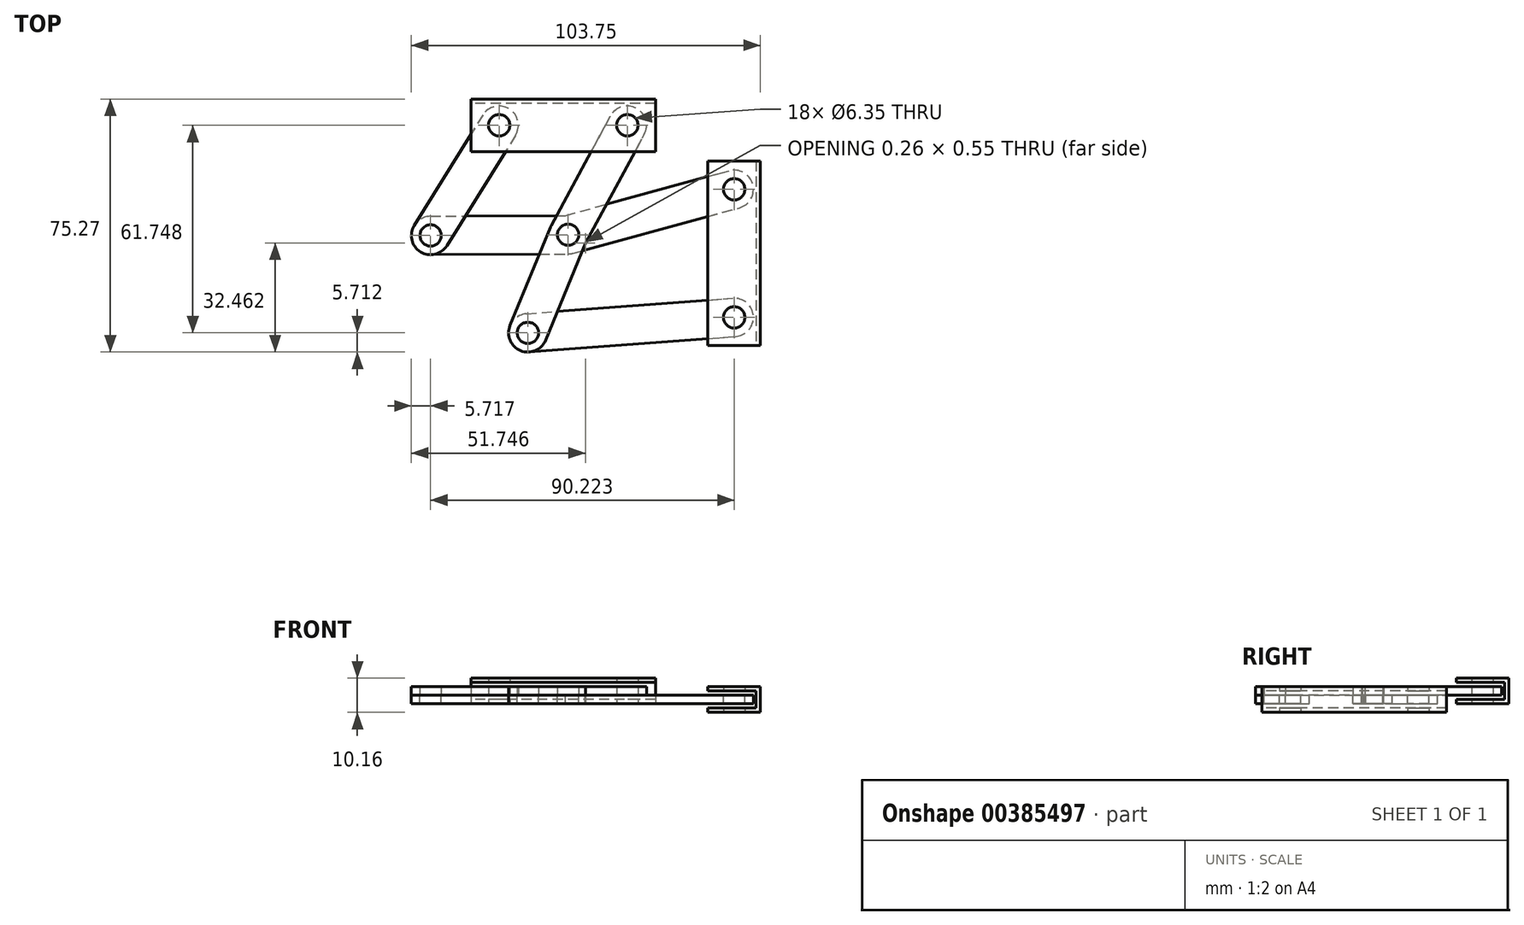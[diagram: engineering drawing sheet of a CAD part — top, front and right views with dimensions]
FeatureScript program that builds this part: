
annotation { "Feature Type Name" : "Feature", "Feature Type Description" : "" }
export const myFeature = defineFeature(function(context is Context, id is Id, definition is map)
    precondition{}
    {
        {
            var Q0;
            Q0=qCreatedBy(makeId("Top.planeOp"),FACE);
            var sketch = newSketch(context, id + "F0", { "sketchPlane" : qUnion([Q0])});
            skCircle(sketch, "E0", {"center": v(-19.05, 0) * mm, "radius": 3.18 * mm});
            skCircle(sketch, "E1", {"center": v(19.05, 0) * mm, "radius": 3.18 * mm});
            skCircle(sketch, "E2", {"center": v(50.8, -19.05) * mm, "radius": 3.18 * mm});
            skCircle(sketch, "E3", {"center": v(50.8, -57.15) * mm, "radius": 3.18 * mm});
            skLineSegment(sketch, "E4", {"start": v(-19.05, 0) * mm, "end": v(19.05, 0) * mm, "construction": true});
            skLineSegment(sketch, "E5", {"start": v(50.8, -19.05) * mm, "end": v(50.8, -57.15) * mm, "construction": true});
            skPoint(sketch, "E6", {"position": v(50.8, -38.1) * mm});
            skPoint(sketch, "E7", {"position": v(0, 0) * mm});
            skSolve(sketch);
        }
        {
            var Q0;
            Q0=qCreatedBy(makeId("Top.planeOp"),FACE);
            var sketch = newSketch(context, id + "F1", { "sketchPlane" : qUnion([Q0])});
            skCircle(sketch, "E8.0", {"center": v(-19.05, 0) * mm, "radius": 3.18 * mm});
            skCircle(sketch, "E9", {"center": v(-39.42, -32.79) * mm, "radius": 3.18 * mm});
            skCircle(sketch, "E10", {"center": v(-19.05, 0) * mm, "radius": 5.72 * mm});
            skCircle(sketch, "E11", {"center": v(-39.42, -32.79) * mm, "radius": 5.72 * mm});
            skLineSegment(sketch, "E12", {"start": v(-23.9, 3.02) * mm, "end": v(-44.28, -29.77) * mm});
            skLineSegment(sketch, "E13", {"start": v(-14.2, -3.02) * mm, "end": v(-34.57, -35.8) * mm});
            skCircle(sketch, "E14.0", {"center": v(50.8, -57.15) * mm, "radius": 3.18 * mm});
            skCircle(sketch, "E15", {"center": v(-10.51, -61.75) * mm, "radius": 3.18 * mm});
            skCircle(sketch, "E16", {"center": v(-10.51, -61.75) * mm, "radius": 5.72 * mm});
            skCircle(sketch, "E17", {"center": v(50.8, -57.15) * mm, "radius": 5.72 * mm});
            skLineSegment(sketch, "E18", {"start": v(-10.94, -56.05) * mm, "end": v(50.37, -51.45) * mm});
            skLineSegment(sketch, "E19", {"start": v(-10.09, -67.45) * mm, "end": v(51.23, -62.85) * mm});
            skCircle(sketch, "E20.0", {"center": v(19.05, 0) * mm, "radius": 3.18 * mm});
            skCircle(sketch, "E21.0", {"center": v(50.8, -19.05) * mm, "radius": 3.18 * mm});
            skCircle(sketch, "E22", {"center": v(19.05, 0) * mm, "radius": 5.72 * mm});
            skCircle(sketch, "E23", {"center": v(50.8, -19.05) * mm, "radius": 5.72 * mm});
            skCircle(sketch, "E24", {"center": v(1.45, -32.56) * mm, "radius": 3.18 * mm});
            skCircle(sketch, "E25", {"center": v(1.45, -32.56) * mm, "radius": 5.72 * mm});
            skLineSegment(sketch, "E26", {"start": v(-3.58, -29.84) * mm, "end": v(14.02, 2.72) * mm});
            skLineSegment(sketch, "E27", {"start": v(6.48, -35.27) * mm, "end": v(24.08, -2.72) * mm});
            skLineSegment(sketch, "E28", {"start": v(2.96, -38.07) * mm, "end": v(52.3, -24.56) * mm});
            skLineSegment(sketch, "E29", {"start": v(-0.06, -27.04) * mm, "end": v(49.3, -13.54) * mm});
            skLineSegment(sketch, "E30", {"start": v(-39.4, -38.5) * mm, "end": v(1.48, -38.27) * mm});
            skLineSegment(sketch, "E31", {"start": v(-39.46, -27.07) * mm, "end": v(1.42, -26.84) * mm});
            skLineSegment(sketch, "E32", {"start": v(-5.22, -63.92) * mm, "end": v(6.74, -34.72) * mm});
            skLineSegment(sketch, "E33", {"start": v(-3.84, -30.39) * mm, "end": v(-15.8, -59.58) * mm});
            skSolve(sketch);
        }
        {
            var Q0;
            {var subQ1=sQuery(id+"F1.wireOp",EDGE,"E22");var subQ8=sQuery(id+"F1.wireOp",EDGE,"E26");var subQ10=makeQuery(id+"F1.imprint","INTERSECT",VERTEX,{"derivedFrom":[subQ1,subQ8]});Q0=makeQuery(id+"F1.imprint","IMPRINT",FACE,{"disambiguationData":[TD([[makeQuery(id+"F1.imprint","IMPRINT",EDGE,{"disambiguationData":[TD([[subQ10,-1.0]])],"derivedFrom":subQ1}),-1.0]])]});}
            var Q1;
            {var subQ0=sQuery(id+"F1.wireOp",EDGE,"E26");var subQ1=sQuery(id+"F1.wireOp",EDGE,"E25");var subQ2=makeQuery(id+"F1.imprint","INTERSECT",VERTEX,{"derivedFrom":[subQ1,subQ0]});Q1=makeQuery(id+"F1.imprint","IMPRINT",FACE,{"disambiguationData":[TD([[makeQuery(id+"F1.imprint","IMPRINT",EDGE,{"disambiguationData":[TD([[subQ2,1.0]])],"derivedFrom":subQ1}),-1.0]])]});}
            var Q2;
            {var subQ0=sQuery(id+"F1.wireOp",EDGE,"E28");var subQ1=sQuery(id+"F1.wireOp",EDGE,"E25");var subQ2=makeQuery(id+"F1.imprint","INTERSECT",VERTEX,{"derivedFrom":[subQ1,subQ0]});Q2=makeQuery(id+"F1.imprint","IMPRINT",FACE,{"disambiguationData":[TD([[makeQuery(id+"F1.imprint","IMPRINT",EDGE,{"disambiguationData":[TD([[subQ2,1.0]])],"derivedFrom":subQ1}),-1.0]])]});}
            var Q3;
            {var subQ0=sQuery(id+"F1.wireOp",EDGE,"E28");var subQ1=sQuery(id+"F1.wireOp",EDGE,"E25");var subQ2=makeQuery(id+"F1.imprint","INTERSECT",VERTEX,{"derivedFrom":[subQ1,subQ0]});Q3=makeQuery(id+"F1.imprint","IMPRINT",FACE,{"disambiguationData":[TD([[makeQuery(id+"F1.imprint","IMPRINT",EDGE,{"disambiguationData":[TD([[subQ2,-1.0]])],"derivedFrom":subQ1}),-1.0]])]});}
            var Q4;
            {var subQ5=sQuery(id+"F1.wireOp",EDGE,"E25");var subQ7=sQuery(id+"F1.wireOp",EDGE,"E27");var subQ8=makeQuery(id+"F1.imprint","INTERSECT",VERTEX,{"derivedFrom":[subQ5,subQ7]});Q4=makeQuery(id+"F1.imprint","IMPRINT",FACE,{"disambiguationData":[TD([[makeQuery(id+"F1.imprint","IMPRINT",EDGE,{"disambiguationData":[TD([[subQ8,1.0]])],"derivedFrom":subQ5}),-1.0]])]});}
            var Q5;
            {var subQ7=sQuery(id+"F1.wireOp",EDGE,"E18");var subQ9=sQuery(id+"F1.wireOp",EDGE,"E16");var subQ10=makeQuery(id+"F1.imprint","INTERSECT",VERTEX,{"derivedFrom":[subQ9,subQ7]});Q5=makeQuery(id+"F1.imprint","IMPRINT",FACE,{"disambiguationData":[TD([[makeQuery(id+"F1.imprint","IMPRINT",EDGE,{"disambiguationData":[TD([[subQ10,-1.0]])],"derivedFrom":subQ9}),-1.0]])]});}
            var Q6;
            {var subQ0=sQuery(id+"F1.wireOp",EDGE,"E29");var subQ1=sQuery(id+"F1.wireOp",EDGE,"E25");var subQ2=makeQuery(id+"F1.imprint","INTERSECT",VERTEX,{"derivedFrom":[subQ1,subQ0]});Q6=makeQuery(id+"F1.imprint","IMPRINT",FACE,{"disambiguationData":[TD([[makeQuery(id+"F1.imprint","IMPRINT",EDGE,{"disambiguationData":[TD([[subQ2,1.0]])],"derivedFrom":subQ1}),-1.0]])]});}
            var Q7;
            {var subQ0=sQuery(id+"F1.wireOp",EDGE,"E18");var subQ1=sQuery(id+"F1.wireOp",EDGE,"E16");var subQ2=makeQuery(id+"F1.imprint","INTERSECT",VERTEX,{"derivedFrom":[subQ1,subQ0]});Q7=makeQuery(id+"F1.imprint","IMPRINT",FACE,{"disambiguationData":[TD([[makeQuery(id+"F1.imprint","IMPRINT",EDGE,{"disambiguationData":[TD([[subQ2,1.0]])],"derivedFrom":subQ1}),-1.0]])]});}
            var Q8;
            Q8=makeQuery(id+"F1.imprint","IMPRINT",FACE,{"disambiguationData":[TD([[makeQuery(id+"F1.imprint","IMPRINT",EDGE,{"derivedFrom":sQuery(id+"F1.wireOp",EDGE,"E15")}),-1.0]])]});
            var Q9;
            Q9=makeQuery(id+"F1.imprint","IMPRINT",FACE,{"disambiguationData":[TD([[makeQuery(id+"F1.imprint","IMPRINT",EDGE,{"derivedFrom":sQuery(id+"F1.wireOp",EDGE,"E20.0")}),-1.0]])]});
            var Q10;
            {var subQ0=sQuery(id+"F1.wireOp",EDGE,"E12");Q10=makeQuery(id+"F1.imprint","IMPRINT",FACE,{"disambiguationData":[TD([[makeQuery(id+"F1.imprint","IMPRINT",EDGE,{"derivedFrom":subQ0}),1.0]])]});}
            var Q11;
            Q11=makeQuery(id+"F1.imprint","IMPRINT",FACE,{"disambiguationData":[TD([[makeQuery(id+"F1.imprint","IMPRINT",EDGE,{"derivedFrom":sQuery(id+"F1.wireOp",EDGE,"E8.0")}),-1.0]])]});
            var Q12;
            Q12=makeQuery(id+"F1.imprint","IMPRINT",FACE,{"disambiguationData":[TD([[makeQuery(id+"F1.imprint","IMPRINT",EDGE,{"derivedFrom":sQuery(id+"F1.wireOp",EDGE,"E9")}),-1.0]])]});
            var Q13;
            {var subQ0=sQuery(id+"F1.wireOp",EDGE,"E13");var subQ1=sQuery(id+"F1.wireOp",EDGE,"E11");var subQ2=makeQuery(id+"F1.imprint","INTERSECT",VERTEX,{"derivedFrom":[subQ1,subQ0]});Q13=makeQuery(id+"F1.imprint","IMPRINT",FACE,{"disambiguationData":[TD([[makeQuery(id+"F1.imprint","IMPRINT",EDGE,{"disambiguationData":[TD([[subQ2,-1.0]])],"derivedFrom":subQ1}),-1.0]])]});}
            var Q14;
            {var subQ0=sQuery(id+"F1.wireOp",EDGE,"E31");var subQ1=sQuery(id+"F1.wireOp",EDGE,"E25");var subQ2=makeQuery(id+"F1.imprint","INTERSECT",VERTEX,{"derivedFrom":[subQ1,subQ0]});Q14=makeQuery(id+"F1.imprint","IMPRINT",FACE,{"disambiguationData":[TD([[makeQuery(id+"F1.imprint","IMPRINT",EDGE,{"disambiguationData":[TD([[subQ2,1.0]])],"derivedFrom":subQ1}),-1.0]])]});}
            var Q15;
            {var subQ0=sQuery(id+"F1.wireOp",EDGE,"E30");var subQ1=sQuery(id+"F1.wireOp",EDGE,"E25");var subQ2=makeQuery(id+"F1.imprint","INTERSECT",VERTEX,{"derivedFrom":[subQ1,subQ0]});Q15=makeQuery(id+"F1.imprint","IMPRINT",FACE,{"disambiguationData":[TD([[makeQuery(id+"F1.imprint","IMPRINT",EDGE,{"disambiguationData":[TD([[subQ2,1.0]])],"derivedFrom":subQ1}),-1.0]])]});}
            extrude(context, id + "F2", {"entities" : qUnion([Q0, Q1, Q2, Q3, Q4, Q5, Q6, Q7, Q8, Q9, Q10, Q11, Q12, Q13, Q14, Q15]), "depth" : 2.54 * mm});
        }
        {
            var Q0;
            Q0=makeQuery(id+"F1.imprint","IMPRINT",FACE,{"disambiguationData":[TD([[makeQuery(id+"F1.imprint","IMPRINT",EDGE,{"derivedFrom":sQuery(id+"F1.wireOp",EDGE,"E24")}),-1.0]])]});
            var Q1;
            {var subQ0=sQuery(id+"F1.wireOp",EDGE,"E27");var subQ1=sQuery(id+"F1.wireOp",EDGE,"E25");var subQ2=makeQuery(id+"F1.imprint","INTERSECT",VERTEX,{"derivedFrom":[subQ1,subQ0]});Q1=makeQuery(id+"F1.imprint","IMPRINT",FACE,{"disambiguationData":[TD([[makeQuery(id+"F1.imprint","IMPRINT",EDGE,{"disambiguationData":[TD([[subQ2,-1.0]])],"derivedFrom":subQ1}),-1.0]])]});}
            var Q2;
            Q2=makeQuery(id+"F2.opExtrude","CAP_FACE",FACE,{"disambiguationData":[OSD([sQuery(id+"F1.wireOp",EDGE,"E20.0"),sQuery(id+"F1.wireOp",EDGE,"E22"),sQuery(id+"F1.wireOp",EDGE,"E25"),sQuery(id+"F1.wireOp",EDGE,"E26"),sQuery(id+"F1.wireOp",EDGE,"E27"),sQuery(id+"F1.wireOp",EDGE,"E32")])],"isStart":false});
            extrude(context, id + "F3", {"entities" : qUnion([Q0, Q1]), "operationType" : NewBodyOperationType.ADD, "endBound" : BoundingType.UP_TO_SURFACE, "endBoundEntityFace" : qUnion([Q2]), "depth" : 25.4 * mm});
        }
        {
            var Q0;
            Q0=makeQuery(id+"F1.imprint","IMPRINT",FACE,{"disambiguationData":[TD([[makeQuery(id+"F1.imprint","IMPRINT",EDGE,{"derivedFrom":sQuery(id+"F1.wireOp",EDGE,"E9")}),-1.0]])]});
            var Q1;
            {var subQ0=sQuery(id+"F1.wireOp",EDGE,"E13");var subQ1=sQuery(id+"F1.wireOp",EDGE,"E11");var subQ2=makeQuery(id+"F1.imprint","INTERSECT",VERTEX,{"derivedFrom":[subQ1,subQ0]});Q1=makeQuery(id+"F1.imprint","IMPRINT",FACE,{"disambiguationData":[TD([[makeQuery(id+"F1.imprint","IMPRINT",EDGE,{"disambiguationData":[TD([[subQ2,-1.0]])],"derivedFrom":subQ1}),-1.0]])]});}
            var Q2;
            {var subQ7=sQuery(id+"F1.wireOp",EDGE,"E13");var subQ8=sQuery(id+"F1.wireOp",EDGE,"E11");var subQ9=makeQuery(id+"F1.imprint","INTERSECT",VERTEX,{"derivedFrom":[subQ8,subQ7]});Q2=makeQuery(id+"F1.imprint","IMPRINT",FACE,{"disambiguationData":[TD([[makeQuery(id+"F1.imprint","IMPRINT",EDGE,{"disambiguationData":[TD([[subQ9,1.0]])],"derivedFrom":subQ8}),-1.0]])]});}
            var Q3;
            {var subQ0=sQuery(id+"F1.wireOp",EDGE,"E26");var subQ1=sQuery(id+"F1.wireOp",EDGE,"E25");var subQ2=makeQuery(id+"F1.imprint","INTERSECT",VERTEX,{"derivedFrom":[subQ1,subQ0]});Q3=makeQuery(id+"F1.imprint","IMPRINT",FACE,{"disambiguationData":[TD([[makeQuery(id+"F1.imprint","IMPRINT",EDGE,{"disambiguationData":[TD([[subQ2,1.0]])],"derivedFrom":subQ1}),-1.0]])]});}
            var Q4;
            {var subQ0=sQuery(id+"F1.wireOp",EDGE,"E29");var subQ1=sQuery(id+"F1.wireOp",EDGE,"E25");var subQ2=makeQuery(id+"F1.imprint","INTERSECT",VERTEX,{"derivedFrom":[subQ1,subQ0]});Q4=makeQuery(id+"F1.imprint","IMPRINT",FACE,{"disambiguationData":[TD([[makeQuery(id+"F1.imprint","IMPRINT",EDGE,{"disambiguationData":[TD([[subQ2,1.0]])],"derivedFrom":subQ1}),-1.0]])]});}
            var Q5;
            {var subQ0=sQuery(id+"F1.wireOp",EDGE,"E28");var subQ1=sQuery(id+"F1.wireOp",EDGE,"E23");var subQ2=makeQuery(id+"F1.imprint","INTERSECT",VERTEX,{"derivedFrom":[subQ1,subQ0]});Q5=makeQuery(id+"F1.imprint","IMPRINT",FACE,{"disambiguationData":[TD([[makeQuery(id+"F1.imprint","IMPRINT",EDGE,{"disambiguationData":[TD([[subQ2,1.0]])],"derivedFrom":subQ1}),-1.0]])]});}
            var Q6;
            {var subQ5=sQuery(id+"F1.wireOp",EDGE,"E25");var subQ7=sQuery(id+"F1.wireOp",EDGE,"E27");var subQ8=makeQuery(id+"F1.imprint","INTERSECT",VERTEX,{"derivedFrom":[subQ5,subQ7]});Q6=makeQuery(id+"F1.imprint","IMPRINT",FACE,{"disambiguationData":[TD([[makeQuery(id+"F1.imprint","IMPRINT",EDGE,{"disambiguationData":[TD([[subQ8,1.0]])],"derivedFrom":subQ5}),-1.0]])]});}
            var Q7;
            {var subQ0=sQuery(id+"F1.wireOp",EDGE,"E28");var subQ1=sQuery(id+"F1.wireOp",EDGE,"E25");var subQ2=makeQuery(id+"F1.imprint","INTERSECT",VERTEX,{"derivedFrom":[subQ1,subQ0]});Q7=makeQuery(id+"F1.imprint","IMPRINT",FACE,{"disambiguationData":[TD([[makeQuery(id+"F1.imprint","IMPRINT",EDGE,{"disambiguationData":[TD([[subQ2,-1.0]])],"derivedFrom":subQ1}),-1.0]])]});}
            var Q8;
            Q8=makeQuery(id+"F1.imprint","IMPRINT",FACE,{"disambiguationData":[TD([[makeQuery(id+"F1.imprint","IMPRINT",EDGE,{"derivedFrom":sQuery(id+"F1.wireOp",EDGE,"E24")}),-1.0]])]});
            var Q9;
            Q9=makeQuery(id+"F1.imprint","IMPRINT",FACE,{"disambiguationData":[TD([[makeQuery(id+"F1.imprint","IMPRINT",EDGE,{"derivedFrom":sQuery(id+"F1.wireOp",EDGE,"E21.0")}),-1.0]])]});
            var Q10;
            Q10=makeQuery(id+"F1.imprint","IMPRINT",FACE,{"disambiguationData":[TD([[makeQuery(id+"F1.imprint","IMPRINT",EDGE,{"derivedFrom":sQuery(id+"F1.wireOp",EDGE,"E14.0")}),-1.0]])]});
            var Q11;
            {var subQ3=sQuery(id+"F1.wireOp",EDGE,"E19");Q11=makeQuery(id+"F1.imprint","IMPRINT",FACE,{"disambiguationData":[TD([[makeQuery(id+"F1.imprint","IMPRINT",EDGE,{"derivedFrom":subQ3}),1.0]])]});}
            var Q12;
            {var subQ0=sQuery(id+"F1.wireOp",EDGE,"E18");var subQ1=sQuery(id+"F1.wireOp",EDGE,"E16");var subQ2=makeQuery(id+"F1.imprint","INTERSECT",VERTEX,{"derivedFrom":[subQ1,subQ0]});Q12=makeQuery(id+"F1.imprint","IMPRINT",FACE,{"disambiguationData":[TD([[makeQuery(id+"F1.imprint","IMPRINT",EDGE,{"disambiguationData":[TD([[subQ2,1.0]])],"derivedFrom":subQ1}),-1.0]])]});}
            var Q13;
            Q13=makeQuery(id+"F1.imprint","IMPRINT",FACE,{"disambiguationData":[TD([[makeQuery(id+"F1.imprint","IMPRINT",EDGE,{"derivedFrom":sQuery(id+"F1.wireOp",EDGE,"E15")}),-1.0]])]});
            var Q14;
            {var subQ0=sQuery(id+"F1.wireOp",EDGE,"E30");var subQ1=sQuery(id+"F1.wireOp",EDGE,"E25");var subQ2=makeQuery(id+"F1.imprint","INTERSECT",VERTEX,{"derivedFrom":[subQ1,subQ0]});Q14=makeQuery(id+"F1.imprint","IMPRINT",FACE,{"disambiguationData":[TD([[makeQuery(id+"F1.imprint","IMPRINT",EDGE,{"disambiguationData":[TD([[subQ2,1.0]])],"derivedFrom":subQ1}),-1.0]])]});}
            var Q15;
            {var subQ0=sQuery(id+"F1.wireOp",EDGE,"E31");var subQ1=sQuery(id+"F1.wireOp",EDGE,"E25");var subQ2=makeQuery(id+"F1.imprint","INTERSECT",VERTEX,{"derivedFrom":[subQ1,subQ0]});Q15=makeQuery(id+"F1.imprint","IMPRINT",FACE,{"disambiguationData":[TD([[makeQuery(id+"F1.imprint","IMPRINT",EDGE,{"disambiguationData":[TD([[subQ2,1.0]])],"derivedFrom":subQ1}),-1.0]])]});}
            extrude(context, id + "F4", {"entities" : qUnion([Q0, Q1, Q2, Q3, Q4, Q5, Q6, Q7, Q8, Q9, Q10, Q11, Q12, Q13, Q14, Q15]), "oppositeDirection" : true, "depth" : 2.54 * mm});
        }
        {
            var Q0;
            Q0=qCreatedBy(makeId("Top.planeOp"),FACE);
            var sketch = newSketch(context, id + "F5", { "sketchPlane" : qUnion([Q0])});
            skLineSegment(sketch, "E34.bottom", {"start": v(27.44, 7.81) * mm, "end": v(-27.44, 7.81) * mm});
            skLineSegment(sketch, "E34.top", {"start": v(27.44, -7.81) * mm, "end": v(-27.44, -7.81) * mm});
            skLineSegment(sketch, "E34.left", {"start": v(27.44, 7.81) * mm, "end": v(27.44, -7.81) * mm});
            skLineSegment(sketch, "E34.right", {"start": v(-27.44, 7.81) * mm, "end": v(-27.44, -7.81) * mm});
            skPoint(sketch, "E34.middle", {"position": v(0, 0) * mm});
            skLineSegment(sketch, "E35.bottom", {"start": v(58.61, -10.66) * mm, "end": v(42.99, -10.66) * mm});
            skLineSegment(sketch, "E35.top", {"start": v(58.61, -65.54) * mm, "end": v(42.99, -65.54) * mm});
            skLineSegment(sketch, "E35.left", {"start": v(58.61, -10.66) * mm, "end": v(58.61, -65.54) * mm});
            skLineSegment(sketch, "E35.right", {"start": v(42.99, -10.66) * mm, "end": v(42.99, -65.54) * mm});
            skPoint(sketch, "E35.middle", {"position": v(50.8, -38.1) * mm});
            skCircle(sketch, "E36.0", {"center": v(19.05, 0) * mm, "radius": 3.18 * mm});
            skCircle(sketch, "E36.1", {"center": v(-19.05, 0) * mm, "radius": 3.18 * mm});
            skCircle(sketch, "E37.0", {"center": v(50.8, -19.05) * mm, "radius": 3.18 * mm});
            skCircle(sketch, "E37.1", {"center": v(50.8, -57.15) * mm, "radius": 3.18 * mm});
            skSolve(sketch);
        }
        {
            var Q0;
            Q0=makeQuery(id+"F5.imprint","IMPRINT",FACE,{"disambiguationData":[TD([[makeQuery(id+"F5.imprint","IMPRINT",EDGE,{"derivedFrom":sQuery(id+"F5.wireOp",EDGE,"E34.bottom")}),1.0]])]});
            extrude(context, id + "F6", {"entities" : qUnion([Q0]), "depth" : 5.08 * mm, "hasSecondDirection" : true, "secondDirectionOppositeDirection" : true, "secondDirectionDepth" : 2.54 * mm});
        }
        {
            var Q0;
            Q0=makeQuery(id+"F5.imprint","IMPRINT",FACE,{"disambiguationData":[TD([[makeQuery(id+"F5.imprint","IMPRINT",EDGE,{"derivedFrom":sQuery(id+"F5.wireOp",EDGE,"E35.bottom")}),1.0]])]});
            extrude(context, id + "F7", {"entities" : qUnion([Q0]), "depth" : 2.54 * mm, "hasSecondDirection" : true, "secondDirectionOppositeDirection" : true, "secondDirectionDepth" : 5.08 * mm});
        }
        {
            var Q0;
            Q0=makeQuery(id+"F6.opExtrude","SWEPT_FACE",FACE,{"disambiguationData":[OSD([sQuery(id+"F5.wireOp",EDGE,"E34.top")])]});
            var Q1;
            Q1=makeQuery(id+"F6.opExtrude","SWEPT_FACE",FACE,{"disambiguationData":[OSD([sQuery(id+"F5.wireOp",EDGE,"E34.left")])]});
            var Q2;
            Q2=makeQuery(id+"F6.opExtrude","SWEPT_FACE",FACE,{"disambiguationData":[OSD([sQuery(id+"F5.wireOp",EDGE,"E34.right")])]});
            var Q3;
            Q3=makeQuery(id+"F6.opExtrude","SWEPT_FACE",FACE,{"disambiguationData":[OSD([sQuery(id+"F5.wireOp",EDGE,"E36.1")])]});
            var Q4;
            Q4=makeQuery(id+"F6.opExtrude","SWEPT_FACE",FACE,{"disambiguationData":[OSD([sQuery(id+"F5.wireOp",EDGE,"E36.0")])]});
            var Q5;
            Q5=makeQuery(id+"F7.opExtrude","SWEPT_FACE",FACE,{"disambiguationData":[OSD([sQuery(id+"F5.wireOp",EDGE,"E35.top")])]});
            var Q6;
            Q6=makeQuery(id+"F7.opExtrude","SWEPT_FACE",FACE,{"disambiguationData":[OSD([sQuery(id+"F5.wireOp",EDGE,"E35.right")])]});
            var Q7;
            Q7=makeQuery(id+"F7.opExtrude","SWEPT_FACE",FACE,{"disambiguationData":[OSD([sQuery(id+"F5.wireOp",EDGE,"E35.bottom")])]});
            var Q8;
            Q8=makeQuery(id+"F7.opExtrude","SWEPT_FACE",FACE,{"disambiguationData":[OSD([sQuery(id+"F5.wireOp",EDGE,"E37.0")])]});
            var Q9;
            Q9=makeQuery(id+"F7.opExtrude","SWEPT_FACE",FACE,{"disambiguationData":[OSD([sQuery(id+"F5.wireOp",EDGE,"E37.1")])]});
            shell(context, id + "F8", {"entities" : qUnion([Q0, Q1, Q2, Q3, Q4, Q5, Q6, Q7, Q8, Q9]), "thickness" : 1.27 * mm});
        }
    });
